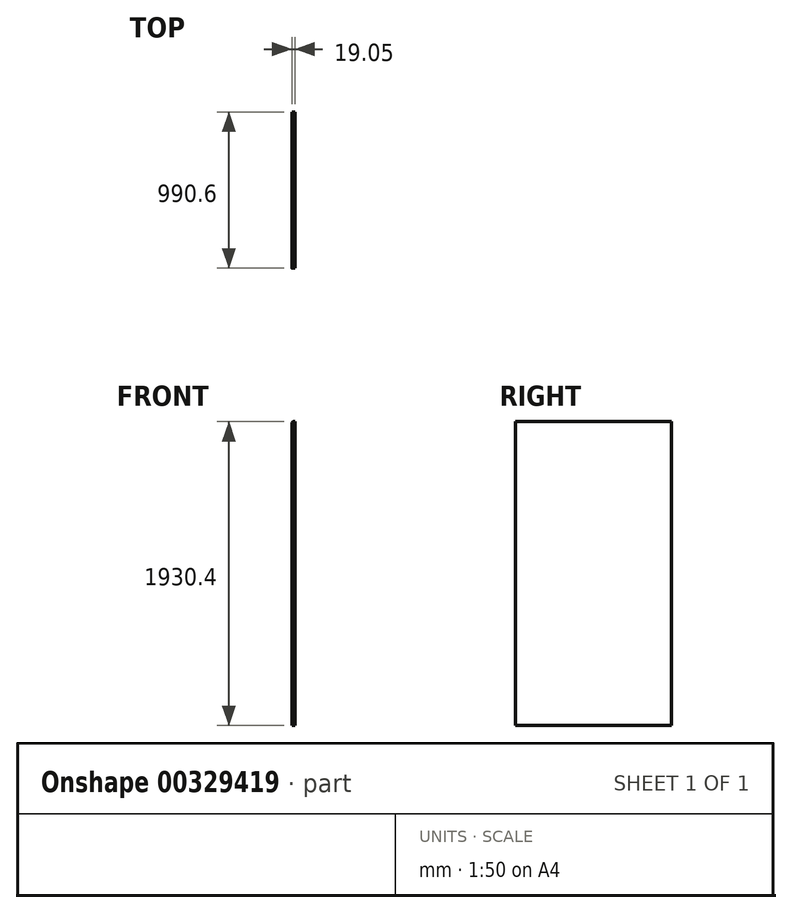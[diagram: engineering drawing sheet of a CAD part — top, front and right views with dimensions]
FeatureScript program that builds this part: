
annotation { "Feature Type Name" : "Feature", "Feature Type Description" : "" }
export const myFeature = defineFeature(function(context is Context, id is Id, definition is map)
    precondition{}
    {
        {
            var Q0;
            Q0=qCreatedBy(makeId("Right.planeOp"),FACE);
            var sketch = newSketch(context, id + "F0", { "sketchPlane" : qUnion([Q0])});
            skLineSegment(sketch, "E0.bottom", {"start": v(495.3, -965.2) * mm, "end": v(-495.3, -965.2) * mm});
            skLineSegment(sketch, "E0.top", {"start": v(495.3, 965.2) * mm, "end": v(-495.3, 965.2) * mm});
            skLineSegment(sketch, "E0.left", {"start": v(495.3, -965.2) * mm, "end": v(495.3, 965.2) * mm});
            skLineSegment(sketch, "E0.right", {"start": v(-495.3, -965.2) * mm, "end": v(-495.3, 965.2) * mm});
            skPoint(sketch, "E0.middle", {"position": v(0, 0) * mm});
            skLineSegment(sketch, "E1", {"start": v(-495.3, 812.8) * mm, "end": v(495.3, 812.8) * mm, "construction": true});
            skSolve(sketch);
        }
        {
            var Q0;
            Q0 = qSketchRegion(id + "F0", true);
            extrude(context, id + "F1", {"entities" : qUnion([Q0]), "depth" : 19.05 * mm});
        }
        {
            var Q0;
            Q0=makeQuery(id+"F1.opExtrude","CAP_EDGE",EDGE,{"disambiguationData":[OSD([sQuery(id+"F0.wireOp",EDGE,"E0.top")])],"isStart":true});
            fillet(context, id + "F2", {"entities" : qUnion([Q0]), "radius" : 12.7 * mm, "tangentPropagation" : true, "allowEdgeOverflow" : false});
        }
    });
